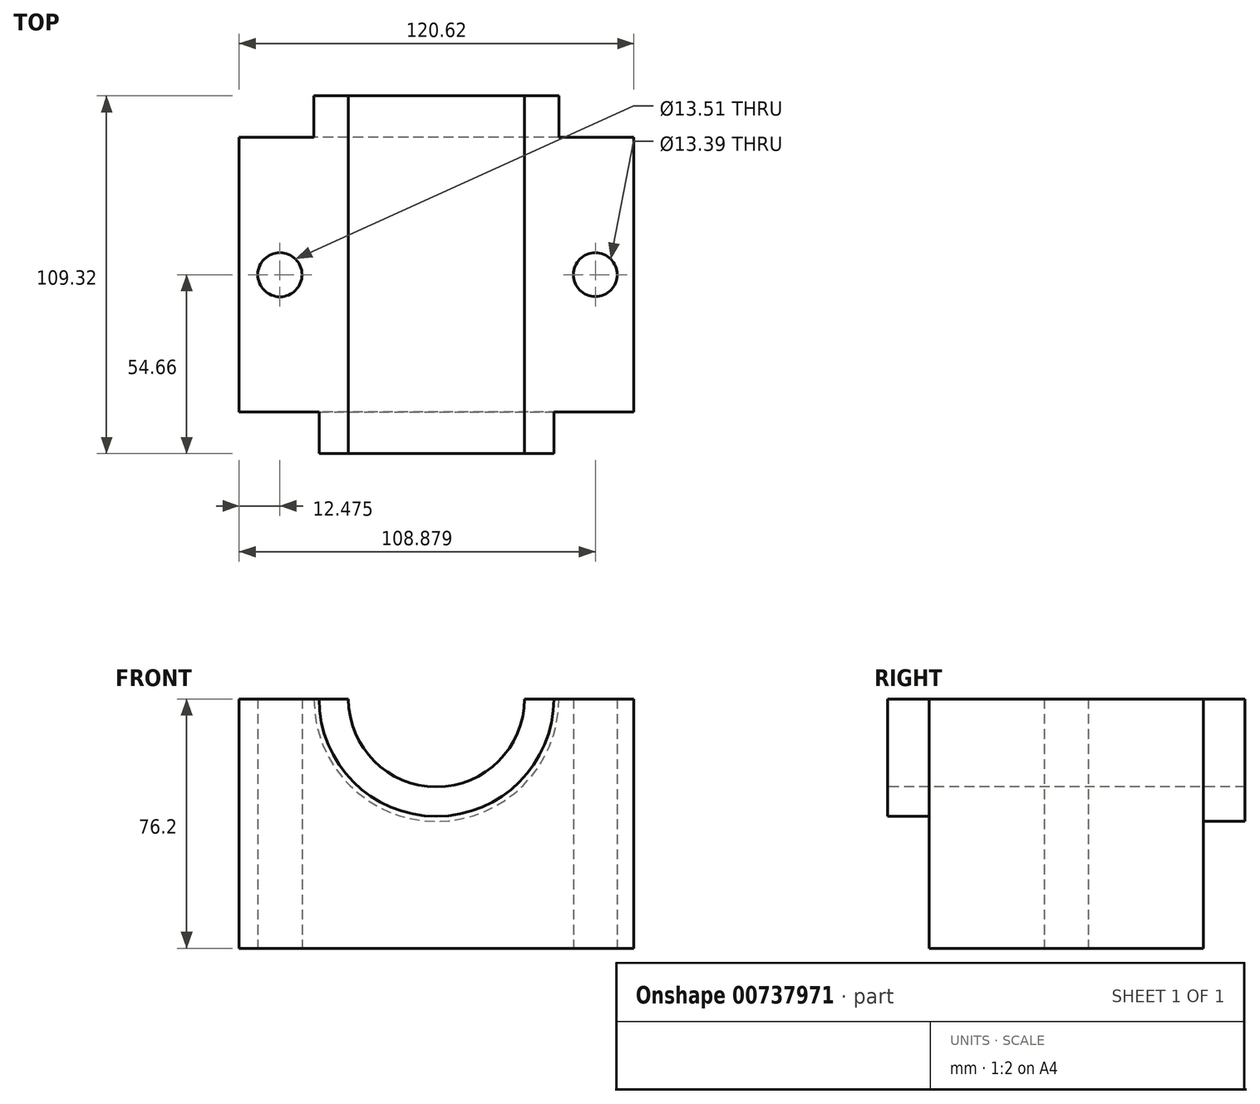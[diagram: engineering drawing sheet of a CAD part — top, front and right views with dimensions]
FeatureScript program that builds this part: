
annotation { "Feature Type Name" : "Feature", "Feature Type Description" : "" }
export const myFeature = defineFeature(function(context is Context, id is Id, definition is map)
    precondition{}
    {
        {
            var Q0;
            Q0=qCreatedBy(makeId("Top.planeOp"),FACE);
            var sketch = newSketch(context, id + "F0", { "sketchPlane" : qUnion([Q0])});
            skLineSegment(sketch, "E0.bottom", {"start": v(60.31, 41.96) * mm, "end": v(-60.31, 41.96) * mm});
            skLineSegment(sketch, "E0.top", {"start": v(60.31, -41.96) * mm, "end": v(-60.31, -41.96) * mm});
            skLineSegment(sketch, "E0.left", {"start": v(60.31, 41.96) * mm, "end": v(60.31, -41.96) * mm});
            skLineSegment(sketch, "E0.right", {"start": v(-60.31, 41.96) * mm, "end": v(-60.31, -41.96) * mm});
            skPoint(sketch, "E0.middle", {"position": v(0, 0) * mm});
            skCircle(sketch, "E1", {"center": v(-47.83, 0) * mm, "radius": 6.76 * mm});
            skCircle(sketch, "E2", {"center": v(48.57, 0) * mm, "radius": 6.7 * mm});
            skSolve(sketch);
        }
        {
            var Q0;
            Q0 = qSketchRegion(id + "F0", true);
            extrude(context, id + "F1", {"entities" : qUnion([Q0]), "depth" : 76.2 * mm, "offsetDistance" : 25.4 * mm});
        }
        {
            var Q0;
            Q0=makeQuery(id+"F1.opExtrude","SWEPT_FACE",FACE,{"disambiguationData":[OSD([sQuery(id+"F0.wireOp",EDGE,"E0.top")])]});
            var sketch = newSketch(context, id + "F2", { "sketchPlane" : qUnion([Q0])});
            skCircle(sketch, "E3", {"center": v(0, 76.2) * mm, "radius": 26.89 * mm});
            skSolve(sketch);
        }
        {
            var Q0;
            Q0 = qSketchRegion(id + "F2", true);
            extrude(context, id + "F3", {"entities" : qUnion([Q0]), "operationType" : NewBodyOperationType.REMOVE, "oppositeDirection" : true, "depth" : 101.6 * mm, "offsetDistance" : 25.4 * mm});
        }
        {
            var Q0;
            Q0=makeQuery(id+"F1.opExtrude","SWEPT_FACE",FACE,{"disambiguationData":[OSD([sQuery(id+"F0.wireOp",EDGE,"E0.top")])]});
            var sketch = newSketch(context, id + "F4", { "sketchPlane" : qUnion([Q0])});
            skArc(sketch, "E4", {"start": v(-35.88, 76.2) * mm, "mid": v(0, 40.32) * mm, "end": v(35.88, 76.2) * mm});
            skLineSegment(sketch, "E5", {"start": v(-35.88, 76.2) * mm, "end": v(-26.89, 76.2) * mm});
            skLineSegment(sketch, "E6", {"start": v(35.88, 76.2) * mm, "end": v(26.89, 76.2) * mm});
            skSolve(sketch);
        }
        {
            var Q0;
            Q0 = qSketchRegion(id + "F4", true);
            var Q1;
            Q1=makeQuery(id+"F4.imprint","IMPRINT",FACE,{"disambiguationData":[TD([[makeQuery(id+"F4.imprint","IMPRINT",EDGE,{"derivedFrom":sQuery(id+"F4.wireOp",EDGE,"E4")}),1.0]])]});
            extrude(context, id + "F5", {"entities" : qUnion([Q0, Q1]), "operationType" : NewBodyOperationType.ADD, "depth" : 12.7 * mm, "offsetDistance" : 25.4 * mm});
        }
        {
            var Q0;
            Q0=makeQuery(id+"F1.opExtrude","SWEPT_FACE",FACE,{"disambiguationData":[OSD([sQuery(id+"F0.wireOp",EDGE,"E0.bottom")])]});
            var sketch = newSketch(context, id + "F6", { "sketchPlane" : qUnion([Q0])});
            skArc(sketch, "E7", {"start": v(-37.44, 76.2) * mm, "mid": v(0, 38.76) * mm, "end": v(37.44, 76.2) * mm});
            skLineSegment(sketch, "E8", {"start": v(-37.44, 76.2) * mm, "end": v(-26.89, 76.2) * mm});
            skLineSegment(sketch, "E9", {"start": v(26.89, 76.2) * mm, "end": v(37.44, 76.2) * mm});
            skSolve(sketch);
        }
        {
            var Q0;
            Q0 = qSketchRegion(id + "F6", true);
            var Q1;
            Q1=makeQuery(id+"F6.imprint","IMPRINT",FACE,{"disambiguationData":[TD([[makeQuery(id+"F6.imprint","IMPRINT",EDGE,{"derivedFrom":sQuery(id+"F6.wireOp",EDGE,"E7")}),1.0]])]});
            extrude(context, id + "F7", {"entities" : qUnion([Q0, Q1]), "operationType" : NewBodyOperationType.ADD, "depth" : 12.7 * mm, "offsetDistance" : 25.4 * mm});
        }
    });
